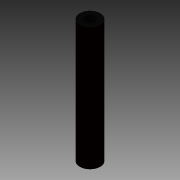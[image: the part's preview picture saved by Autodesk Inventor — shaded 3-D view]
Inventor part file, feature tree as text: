
AUTODESK INVENTOR PART (.ipt)
format: ipt  version: 2013 (Build 170138000, 138)  size: 82,432 bytes
history: native  units: in
note: dims shown in document units (in); Inventor stores cm internally (conversion verified against a paired STEP export)
features: extrude x1, sketch x1
ambient origin geometry x8: Origin, YZ Plane, XZ Plane, XY Plane, X Axis, Y Axis, Z Axis, Center Point
bodies: Solid1 (feature_tree)
feature tree (2):
  extrude  "Extrusion1"  Depth=0.25in
  sketch  "Sketch1"  dims[d0=0.5in d1=0.25in d2=3.0in d3=0.0in]
